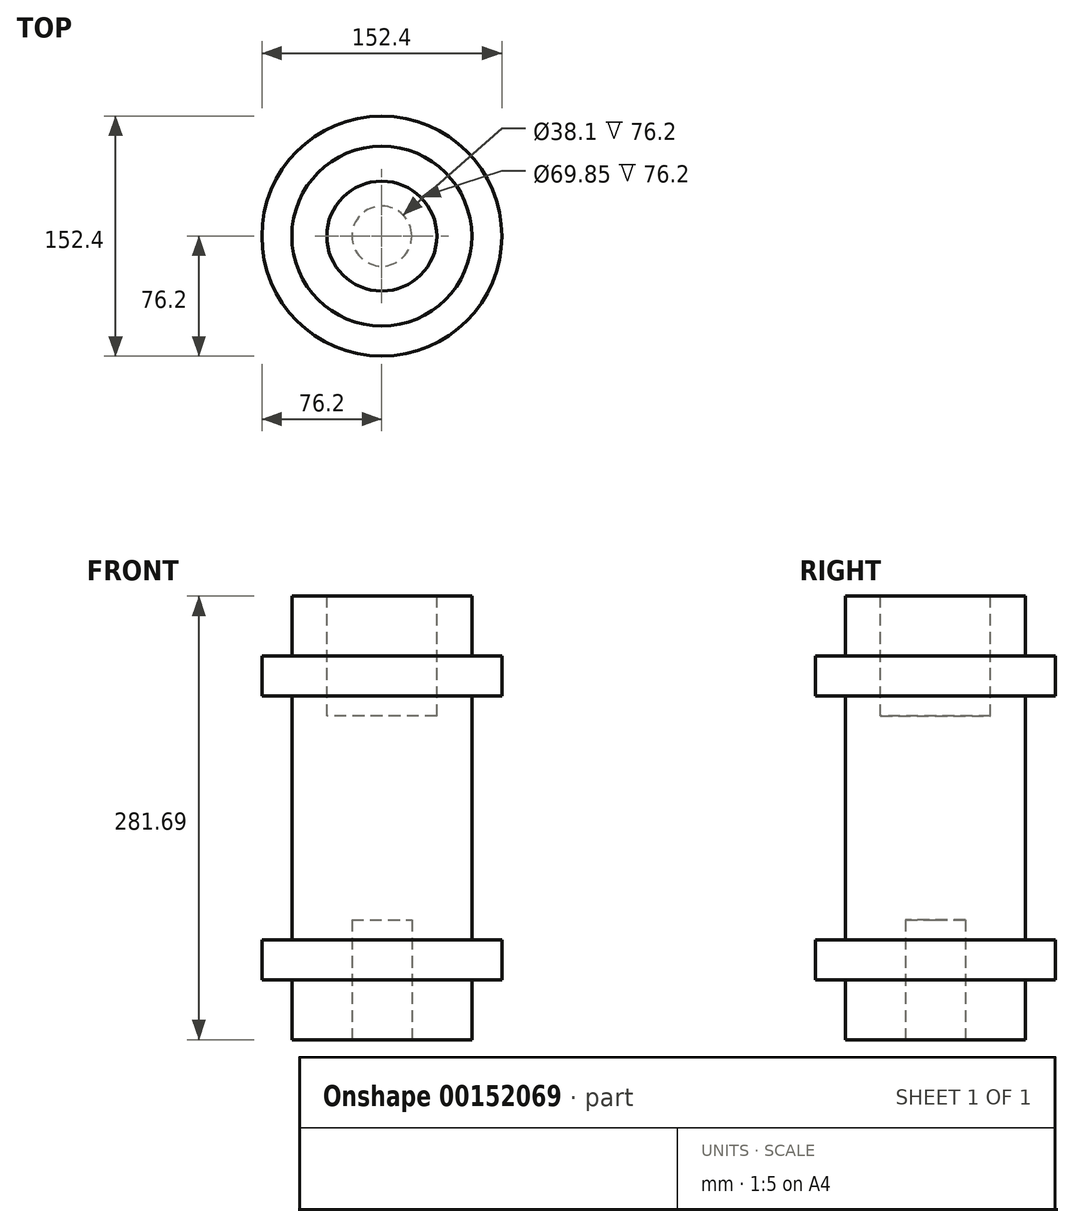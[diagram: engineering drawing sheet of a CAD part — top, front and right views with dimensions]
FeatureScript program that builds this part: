
annotation { "Feature Type Name" : "Feature", "Feature Type Description" : "" }
export const myFeature = defineFeature(function(context is Context, id is Id, definition is map)
    precondition{}
    {
        {
            var Q0;
            Q0=qCreatedBy(makeId("Front.planeOp"),FACE);
            var sketch = newSketch(context, id + "F0", { "sketchPlane" : qUnion([Q0])});
            skLineSegment(sketch, "E0", {"start": v(0, 0) * mm, "end": v(0, 180.09) * mm});
            skLineSegment(sketch, "E1", {"start": v(0, 180.09) * mm, "end": v(76.2, 180.09) * mm});
            skLineSegment(sketch, "E2", {"start": v(76.2, 180.09) * mm, "end": v(76.2, 167.39) * mm});
            skLineSegment(sketch, "E3", {"start": v(76.2, 167.39) * mm, "end": v(57.15, 167.39) * mm});
            skLineSegment(sketch, "E4", {"start": v(57.15, 167.39) * mm, "end": v(57.15, 12.7) * mm});
            skLineSegment(sketch, "E5", {"start": v(57.15, 12.7) * mm, "end": v(76.2, 12.7) * mm});
            skLineSegment(sketch, "E6", {"start": v(76.2, 12.7) * mm, "end": v(76.2, 0) * mm});
            skLineSegment(sketch, "E7", {"start": v(76.2, 0) * mm, "end": v(0, 0) * mm});
            skLineSegment(sketch, "E8", {"start": v(0, 0) * mm, "end": v(76.2, 0) * mm});
            skLineSegment(sketch, "E9", {"start": v(76.2, 0) * mm, "end": v(76.2, -12.7) * mm});
            skLineSegment(sketch, "E10", {"start": v(76.2, -12.7) * mm, "end": v(57.15, -12.7) * mm});
            skLineSegment(sketch, "E11", {"start": v(57.15, -12.7) * mm, "end": v(57.15, -50.8) * mm});
            skLineSegment(sketch, "E12", {"start": v(57.15, -50.8) * mm, "end": v(0, -50.8) * mm});
            skLineSegment(sketch, "E13", {"start": v(0, -50.8) * mm, "end": v(0, 0) * mm});
            skLineSegment(sketch, "E14", {"start": v(76.2, 180.09) * mm, "end": v(76.2, 192.79) * mm});
            skLineSegment(sketch, "E15", {"start": v(76.2, 192.79) * mm, "end": v(57.15, 192.79) * mm});
            skLineSegment(sketch, "E16", {"start": v(57.15, 192.79) * mm, "end": v(57.15, 230.89) * mm});
            skLineSegment(sketch, "E17", {"start": v(57.15, 230.89) * mm, "end": v(0, 230.89) * mm});
            skLineSegment(sketch, "E18", {"start": v(0, 230.89) * mm, "end": v(0, 180.09) * mm});
            skSolve(sketch);
        }
        {
            var Q0;
            Q0 = qSketchRegion(id + "F0", true);
            var Q1;
            Q1=sQuery(id+"F0.wireOp",EDGE,"E0");
            revolve(context, id + "F1", {"entities" : qUnion([Q0]), "axis" : qUnion([Q1]), "revolveType" : RevolveType.FULL});
        }
        {
            var Q0;
            Q0=makeQuery(id+"F1.opRevolve","SWEPT_FACE",FACE,{"disambiguationData":[OSD([sQuery(id+"F0.wireOp",EDGE,"E12")])]});
            var sketch = newSketch(context, id + "F2", { "sketchPlane" : qUnion([Q0])});
            skCircle(sketch, "E19", {"center": v(0, 0) * mm, "radius": 19.05 * mm});
            skSolve(sketch);
        }
        {
            var Q0;
            Q0 = qSketchRegion(id + "F2", true);
            extrude(context, id + "F3", {"entities" : qUnion([Q0]), "operationType" : NewBodyOperationType.REMOVE, "oppositeDirection" : true, "depth" : 76.2 * mm});
        }
        {
            var Q0;
            Q0=makeQuery(id+"F1.opRevolve","SWEPT_FACE",FACE,{"disambiguationData":[OSD([sQuery(id+"F0.wireOp",EDGE,"E17")])]});
            var sketch = newSketch(context, id + "F4", { "sketchPlane" : qUnion([Q0])});
            skCircle(sketch, "E20", {"center": v(0, 0) * mm, "radius": 34.93 * mm});
            skSolve(sketch);
        }
        {
            var Q0;
            Q0 = qSketchRegion(id + "F4", true);
            extrude(context, id + "F5", {"entities" : qUnion([Q0]), "operationType" : NewBodyOperationType.REMOVE, "oppositeDirection" : true, "depth" : 76.2 * mm});
        }
    });
